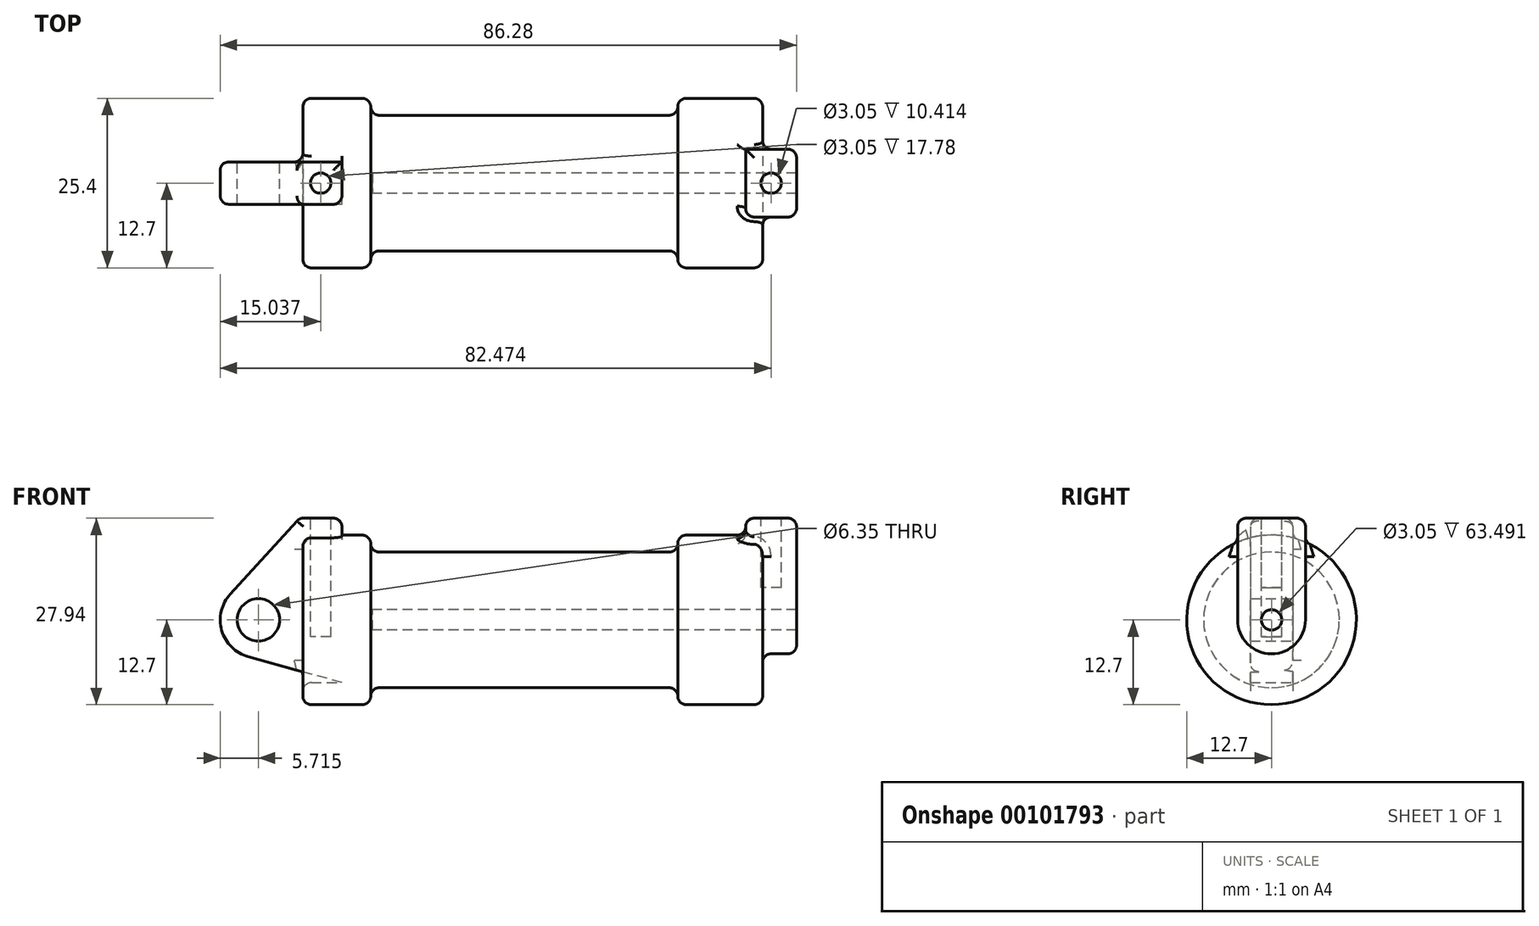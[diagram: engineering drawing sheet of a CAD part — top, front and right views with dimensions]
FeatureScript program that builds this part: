
annotation { "Feature Type Name" : "Feature", "Feature Type Description" : "" }
export const myFeature = defineFeature(function(context is Context, id is Id, definition is map)
    precondition{}
    {
        {
            var Q0;
            Q0=qCreatedBy(makeId("Front.planeOp"),FACE);
            var sketch = newSketch(context, id + "F0", { "sketchPlane" : qUnion([Q0])});
            skLineSegment(sketch, "E0", {"start": v(0, 0) * mm, "end": v(0, 12.7) * mm});
            skLineSegment(sketch, "E1", {"start": v(0, 12.7) * mm, "end": v(10.16, 12.7) * mm});
            skLineSegment(sketch, "E2", {"start": v(10.16, 12.7) * mm, "end": v(10.16, 10.16) * mm});
            skLineSegment(sketch, "E3", {"start": v(10.16, 10.16) * mm, "end": v(56.13, 10.16) * mm});
            skLineSegment(sketch, "E4", {"start": v(56.13, 10.16) * mm, "end": v(56.13, 12.7) * mm});
            skLineSegment(sketch, "E5", {"start": v(56.13, 12.7) * mm, "end": v(66.3, 12.7) * mm});
            skLineSegment(sketch, "E6", {"start": v(66.3, 12.7) * mm, "end": v(66.3, 0) * mm});
            skLineSegment(sketch, "E7", {"start": v(66.3, 0) * mm, "end": v(0, 0) * mm});
            skLineSegment(sketch, "E8", {"start": v(5.84, 15.24) * mm, "end": v(-0.5, 15.24) * mm});
            skLineSegment(sketch, "E9", {"start": v(-0.5, 15.24) * mm, "end": v(-10.88, 3.85) * mm});
            skLineSegment(sketch, "E10", {"start": v(0, 0) * mm, "end": v(-6.65, 0) * mm});
            skCircle(sketch, "E11", {"center": v(-6.65, 0) * mm, "radius": 5.72 * mm});
            skCircle(sketch, "E12", {"center": v(-6.65, 0) * mm, "radius": 3.18 * mm});
            skLineSegment(sketch, "E13", {"start": v(5.84, 15.24) * mm, "end": v(5.84, -9.4) * mm});
            skLineSegment(sketch, "E14", {"start": v(5.84, -9.4) * mm, "end": v(-8.18, -5.5) * mm});
            skSolve(sketch);
        }
        {
            var Q0;
            {var subQ0=sQuery(id+"F0.wireOp",EDGE,"E2");Q0=makeQuery(id+"F0.imprint","IMPRINT",FACE,{"disambiguationData":[TD([[makeQuery(id+"F0.imprint","IMPRINT",EDGE,{"derivedFrom":subQ0}),-1.0]])]});}
            var Q1;
            Q1=sQuery(id+"F0.wireOp",EDGE,"E7");
            revolve(context, id + "F1", {"entities" : qUnion([Q0]), "axis" : qUnion([Q1]), "revolveType" : RevolveType.FULL});
        }
        {
            var Q0;
            {var subQ3=sQuery(id+"F0.wireOp",EDGE,"E0");Q0=makeQuery(id+"F0.imprint","IMPRINT",FACE,{"disambiguationData":[TD([[makeQuery(id+"F0.imprint","IMPRINT",EDGE,{"derivedFrom":subQ3}),1.0]])]});}
            var Q1;
            {var subQ0=sQuery(id+"F0.wireOp",EDGE,"E0");Q1=makeQuery(id+"F0.imprint","IMPRINT",FACE,{"disambiguationData":[TD([[makeQuery(id+"F0.imprint","IMPRINT",EDGE,{"derivedFrom":subQ0}),-1.0]])]});}
            var Q2;
            {var subQ0=sQuery(id+"F0.wireOp",EDGE,"E14");Q2=makeQuery(id+"F0.imprint","IMPRINT",FACE,{"disambiguationData":[TD([[makeQuery(id+"F0.imprint","IMPRINT",EDGE,{"derivedFrom":subQ0}),-1.0]])]});}
            var Q3;
            {var subQ4=sQuery(id+"F0.wireOp",EDGE,"E12");Q3=makeQuery(id+"F0.imprint","IMPRINT",FACE,{"disambiguationData":[TD([[makeQuery(id+"F0.imprint","IMPRINT",EDGE,{"derivedFrom":subQ4}),-1.0]])]});}
            extrude(context, id + "F2", {"entities" : qUnion([Q0, Q1, Q2, Q3]), "operationType" : NewBodyOperationType.ADD, "depth" : 3.17 * mm, "hasSecondDirection" : true, "secondDirectionOppositeDirection" : true, "secondDirectionDepth" : 3.17 * mm});
        }
        {
            var Q0;
            Q0=makeQuery(id+"F1.opRevolve","SWEPT_FACE",FACE,{"disambiguationData":[OSD([sQuery(id+"F0.wireOp",EDGE,"E13")])]});
            extrude(context, id + "F3", {"entities" : qUnion([Q0]), "operationType" : NewBodyOperationType.ADD, "depth" : 5.84 * mm});
        }
        {
            var Q0;
            Q0=makeQuery(id+"F1.opRevolve","SWEPT_FACE",FACE,{"disambiguationData":[OSD([sQuery(id+"F0.wireOp",EDGE,"E6")])]});
            var sketch = newSketch(context, id + "F4", { "sketchPlane" : qUnion([Q0])});
            skCircle(sketch, "E15", {"center": v(0, 0) * mm, "radius": 1.52 * mm});
            skCircle(sketch, "E16", {"center": v(0, 0) * mm, "radius": 5.08 * mm});
            skLineSegment(sketch, "E17", {"start": v(-5.08, 0) * mm, "end": v(-5.08, 15.24) * mm});
            skLineSegment(sketch, "E18", {"start": v(-5.08, 15.24) * mm, "end": v(5.08, 15.24) * mm});
            skLineSegment(sketch, "E19", {"start": v(5.08, 15.24) * mm, "end": v(5.08, 0) * mm});
            skSolve(sketch);
        }
        {
            var Q0;
            Q0=makeQuery(id+"F4.imprint","IMPRINT",FACE,{"disambiguationData":[TD([[makeQuery(id+"F4.imprint","IMPRINT",EDGE,{"derivedFrom":sQuery(id+"F4.wireOp",EDGE,"E15")}),-1.0]])]});
            var Q1;
            {var subQ0=sQuery(id+"F4.wireOp",EDGE,"E17");var subQ1=sQuery(id+"F4.wireOp",EDGE,"E16");var subQ2=makeQuery(id+"F4.imprint","INTERSECT",VERTEX,{"derivedFrom":[subQ1,subQ0]});Q1=makeQuery(id+"F4.imprint","IMPRINT",FACE,{"disambiguationData":[TD([[makeQuery(id+"F4.imprint","IMPRINT",EDGE,{"disambiguationData":[TD([[subQ2,1.0]])],"derivedFrom":subQ1}),-1.0]])]});}
            var Q2;
            {var subQ0=sQuery(id+"F4.wireOp",EDGE,"E18");Q2=makeQuery(id+"F4.imprint","IMPRINT",FACE,{"disambiguationData":[TD([[makeQuery(id+"F4.imprint","IMPRINT",EDGE,{"derivedFrom":subQ0}),-1.0]])]});}
            extrude(context, id + "F5", {"entities" : qUnion([Q0, Q1, Q2]), "operationType" : NewBodyOperationType.ADD, "depth" : 7.62 * mm});
        }
        {
            var Q0;
            Q0=makeQuery(id+"F5.boolean.opBoolean","SPLIT",FACE,{"disambiguationData":[TD([makeQuery(id+"F1.opRevolve","SWEPT_FACE",FACE,{"disambiguationData":[OSD([sQuery(id+"F0.wireOp",EDGE,"E5")])]})])],"derivedFrom":makeQuery(id+"F1.opRevolve","SWEPT_FACE",FACE,{"disambiguationData":[OSD([sQuery(id+"F0.wireOp",EDGE,"E6")])]})});
            extrude(context, id + "F6", {"entities" : qUnion([Q0]), "operationType" : NewBodyOperationType.ADD, "depth" : 2.54 * mm});
        }
        {
            var Q0;
            Q0=makeQuery(id+"F5.boolean.opBoolean","SPLIT",FACE,{"disambiguationData":[TD([makeQuery(id+"F5.opExtrude","SWEPT_FACE",FACE,{"disambiguationData":[OSD([sQuery(id+"F4.wireOp",EDGE,"E15")])]})])],"derivedFrom":makeQuery(id+"F1.opRevolve","SWEPT_FACE",FACE,{"disambiguationData":[OSD([sQuery(id+"F0.wireOp",EDGE,"E6")])]})});
            extrude(context, id + "F7", {"entities" : qUnion([Q0]), "operationType" : NewBodyOperationType.REMOVE, "oppositeDirection" : true, "depth" : 55.87 * mm});
        }
        {
            var Q0;
            Q0=makeQuery(id+"F2.opExtrude","SWEPT_FACE",FACE,{"disambiguationData":[OSD([sQuery(id+"F0.wireOp",EDGE,"E8")])]});
            var sketch = newSketch(context, id + "F8", { "sketchPlane" : qUnion([Q0])});
            skCircle(sketch, "E20", {"center": v(2.67, 0) * mm, "radius": 1.52 * mm});
            skPoint(sketch, "E20.centerSnap0", {"position": v(5.84, 0) * mm});
            skPoint(sketch, "E20.centerSnap1", {"position": v(2.67, 3.18) * mm});
            skSolve(sketch);
        }
        {
            var Q0;
            Q0=makeQuery(id+"F5.opExtrude","SWEPT_FACE",FACE,{"disambiguationData":[OSD([sQuery(id+"F4.wireOp",EDGE,"E18")])]});
            var sketch = newSketch(context, id + "F9", { "sketchPlane" : qUnion([Q0])});
            skCircle(sketch, "E21", {"center": v(70.1, 0) * mm, "radius": 1.52 * mm});
            skPoint(sketch, "E21.centerSnap0", {"position": v(73.91, 0) * mm});
            skPoint(sketch, "E21.centerSnap1", {"position": v(70.1, 5.08) * mm});
            skSolve(sketch);
        }
        {
            var Q0;
            Q0=makeQuery(id+"F9.imprint","IMPRINT",FACE,{"disambiguationData":[TD([[makeQuery(id+"F9.imprint","IMPRINT",EDGE,{"derivedFrom":sQuery(id+"F9.wireOp",EDGE,"E21")}),1.0]])]});
            extrude(context, id + "F10", {"entities" : qUnion([Q0]), "operationType" : NewBodyOperationType.REMOVE, "oppositeDirection" : true, "depth" : 10.4 * mm});
        }
        {
            var Q0;
            Q0=makeQuery(id+"F8.imprint","IMPRINT",FACE,{"disambiguationData":[TD([[makeQuery(id+"F8.imprint","IMPRINT",EDGE,{"derivedFrom":sQuery(id+"F8.wireOp",EDGE,"E20")}),1.0]])]});
            extrude(context, id + "F11", {"entities" : qUnion([Q0]), "operationType" : NewBodyOperationType.REMOVE, "oppositeDirection" : true, "depth" : 17.78 * mm});
        }
        {
            var Q0;
            Q0=makeQuery(id+"F2.opExtrude","CAP_EDGE",EDGE,{"disambiguationData":[OSD([sQuery(id+"F0.wireOp",EDGE,"E9")])],"isStart":false});
            var Q1;
            Q1=makeQuery(id+"F2.opExtrude","CAP_EDGE",EDGE,{"disambiguationData":[OSD([sQuery(id+"F0.wireOp",EDGE,"E11")])],"isStart":false});
            var Q2;
            {var subQ0=sQuery(id+"F0.wireOp",EDGE,"E14");Q2=makeQuery(id+"F3.boolean.opBoolean","SPLIT",EDGE,{"disambiguationData":[topologyDisambiguationEdgeConnected([makeQuery(id+"F2.opExtrude","CAP_FACE",FACE,{"disambiguationData":[OSD([sQuery(id+"F0.wireOp",EDGE,"E8"),sQuery(id+"F0.wireOp",EDGE,"E9"),sQuery(id+"F0.wireOp",EDGE,"E11"),sQuery(id+"F0.wireOp",EDGE,"E12"),sQuery(id+"F0.wireOp",EDGE,"E13"),subQ0])],"isStart":false})])],"derivedFrom":makeQuery(id+"F2.opExtrude","CAP_EDGE",EDGE,{"disambiguationData":[OSD([subQ0])],"isStart":false})});}
            var Q3;
            Q3=makeQuery(id+"F3.opExtrude","CAP_EDGE",EDGE,{"disambiguationData":[OSD([sQuery(id+"F0.wireOp",EDGE,"E1"),sQuery(id+"F0.wireOp",EDGE,"E13")])],"isStart":false});
            var Q4;
            Q4=makeQuery(id+"F1.opRevolve","SWEPT_EDGE",EDGE,{"disambiguationData":[OSD([sQuery(id+"F0.wireOp",EDGE,"E1"),sQuery(id+"F0.wireOp",EDGE,"E2")])]});
            fillet(context, id + "F12", {"entities" : qUnion([Q0, Q1, Q2, Q3, Q4]), "radius" : 1.27 * mm, "tangentPropagation" : true, "allowEdgeOverflow" : false});
        }
        {
            var Q0;
            Q0=makeQuery(id+"F2.opExtrude","CAP_EDGE",EDGE,{"disambiguationData":[OSD([sQuery(id+"F0.wireOp",EDGE,"E9")])],"isStart":true});
            var Q1;
            Q1=makeQuery(id+"F2.opExtrude","CAP_EDGE",EDGE,{"disambiguationData":[OSD([sQuery(id+"F0.wireOp",EDGE,"E11")])],"isStart":true});
            var Q2;
            {var subQ0=sQuery(id+"F0.wireOp",EDGE,"E14");Q2=makeQuery(id+"F3.boolean.opBoolean","SPLIT",EDGE,{"disambiguationData":[topologyDisambiguationEdgeConnected([makeQuery(id+"F2.opExtrude","CAP_FACE",FACE,{"disambiguationData":[OSD([sQuery(id+"F0.wireOp",EDGE,"E8"),sQuery(id+"F0.wireOp",EDGE,"E9"),sQuery(id+"F0.wireOp",EDGE,"E11"),sQuery(id+"F0.wireOp",EDGE,"E12"),sQuery(id+"F0.wireOp",EDGE,"E13"),subQ0])],"isStart":true})])],"derivedFrom":makeQuery(id+"F2.opExtrude","CAP_EDGE",EDGE,{"disambiguationData":[OSD([subQ0])],"isStart":true})});}
            var Q3;
            Q3=makeQuery(id+"F2.opExtrude","CAP_EDGE",EDGE,{"disambiguationData":[OSD([sQuery(id+"F0.wireOp",EDGE,"E8")])],"isStart":true});
            var Q4;
            Q4=makeQuery(id+"F2.opExtrude","SWEPT_EDGE",EDGE,{"disambiguationData":[OSD([sQuery(id+"F0.wireOp",EDGE,"E8"),sQuery(id+"F0.wireOp",EDGE,"E13")])]});
            var Q5;
            {var subQ0=sQuery(id+"F0.wireOp",EDGE,"E1");var subQ1=sQuery(id+"F0.wireOp",EDGE,"E13");Q5=makeQuery(id+"F2.boolean.opBoolean","SPLIT",EDGE,{"disambiguationData":[topologyDisambiguationEdgeConnected([makeQuery(id+"F2.opExtrude","SWEPT_FACE",FACE,{"disambiguationData":[OSD([subQ1])]})])],"derivedFrom":makeQuery(id+"F1.opRevolve","SWEPT_EDGE",EDGE,{"disambiguationData":[OSD([subQ0,subQ1])]})});}
            fillet(context, id + "F13", {"entities" : qUnion([Q0, Q1, Q2, Q3, Q4, Q5]), "radius" : 1.27 * mm, "tangentPropagation" : true, "allowEdgeOverflow" : false});
        }
        {
            var Q0;
            Q0=makeQuery(id+"F2.opExtrude","CAP_EDGE",EDGE,{"disambiguationData":[OSD([sQuery(id+"F0.wireOp",EDGE,"E8")])],"isStart":false});
            var Q1;
            Q1=makeQuery(id+"F1.opRevolve","SWEPT_EDGE",EDGE,{"disambiguationData":[OSD([sQuery(id+"F0.wireOp",EDGE,"E4"),sQuery(id+"F0.wireOp",EDGE,"E5")])]});
            var Q2;
            Q2=makeQuery(id+"F6.opExtrude","CAP_EDGE",EDGE,{"disambiguationData":[OSD([sQuery(id+"F0.wireOp",EDGE,"E5"),sQuery(id+"F0.wireOp",EDGE,"E6")])],"isStart":false});
            var Q3;
            {var subQ0=sQuery(id+"F4.wireOp",EDGE,"E17");Q3=makeQuery(id+"F5.boolean.opBoolean","SPLIT",EDGE,{"disambiguationData":[topologyDisambiguationEdgeConnected([makeQuery(id+"F5.opExtrude","CAP_FACE",FACE,{"disambiguationData":[OSD([sQuery(id+"F4.wireOp",EDGE,"E15"),sQuery(id+"F4.wireOp",EDGE,"E16"),subQ0,sQuery(id+"F4.wireOp",EDGE,"E18"),sQuery(id+"F4.wireOp",EDGE,"E19")])],"isStart":true})])],"derivedFrom":makeQuery(id+"F5.opExtrude","CAP_EDGE",EDGE,{"disambiguationData":[OSD([subQ0])],"isStart":true})});}
            var Q4;
            Q4=makeQuery(id+"F5.opExtrude","CAP_EDGE",EDGE,{"disambiguationData":[OSD([sQuery(id+"F4.wireOp",EDGE,"E16")])],"isStart":false});
            var Q5;
            Q5=makeQuery(id+"F5.opExtrude","CAP_EDGE",EDGE,{"disambiguationData":[OSD([sQuery(id+"F4.wireOp",EDGE,"E17")])],"isStart":false});
            var Q6;
            Q6=makeQuery(id+"F5.opExtrude","CAP_EDGE",EDGE,{"disambiguationData":[OSD([sQuery(id+"F4.wireOp",EDGE,"E19")])],"isStart":false});
            var Q7;
            Q7=makeQuery(id+"F5.opExtrude","CAP_EDGE",EDGE,{"disambiguationData":[OSD([sQuery(id+"F4.wireOp",EDGE,"E18")])],"isStart":false});
            var Q8;
            Q8=makeQuery(id+"F5.opExtrude","SWEPT_EDGE",EDGE,{"disambiguationData":[OSD([sQuery(id+"F4.wireOp",EDGE,"E17"),sQuery(id+"F4.wireOp",EDGE,"E18")])]});
            var Q9;
            Q9=makeQuery(id+"F5.opExtrude","CAP_EDGE",EDGE,{"disambiguationData":[OSD([sQuery(id+"F4.wireOp",EDGE,"E18")])],"isStart":true});
            var Q10;
            Q10=makeQuery(id+"F5.opExtrude","SWEPT_EDGE",EDGE,{"disambiguationData":[OSD([sQuery(id+"F4.wireOp",EDGE,"E18"),sQuery(id+"F4.wireOp",EDGE,"E19")])]});
            fillet(context, id + "F14", {"entities" : qUnion([Q0, Q1, Q2, Q3, Q4, Q5, Q6, Q7, Q8, Q9, Q10]), "radius" : 1.27 * mm, "tangentPropagation" : true, "allowEdgeOverflow" : false});
        }
        {
            var Q0;
            Q0=makeQuery(id+"F1.opRevolve","SWEPT_EDGE",EDGE,{"disambiguationData":[OSD([sQuery(id+"F0.wireOp",EDGE,"E3"),sQuery(id+"F0.wireOp",EDGE,"E4")])]});
            var Q1;
            Q1=makeQuery(id+"F1.opRevolve","SWEPT_EDGE",EDGE,{"disambiguationData":[OSD([sQuery(id+"F0.wireOp",EDGE,"E2"),sQuery(id+"F0.wireOp",EDGE,"E3")])]});
            fillet(context, id + "F15", {"entities" : qUnion([Q0, Q1]), "radius" : 1.27 * mm, "tangentPropagation" : true, "allowEdgeOverflow" : false});
        }
        {
            var Q0;
            Q0=makeQuery(id+"F14.opFillet","BLEND_EDGE",EDGE,{"blendedFrom":[makeQuery(id+"F6.opExtrude","CAP_EDGE",EDGE,{"disambiguationData":[OSD([sQuery(id+"F0.wireOp",EDGE,"E5"),sQuery(id+"F0.wireOp",EDGE,"E6")])],"isStart":false}),makeQuery(id+"F5.opExtrude","SWEPT_FACE",FACE,{"disambiguationData":[OSD([sQuery(id+"F4.wireOp",EDGE,"E17")])]})],"blendedInto":[makeQuery(id+"F5.opExtrude","SWEPT_FACE",FACE,{"disambiguationData":[OSD([sQuery(id+"F4.wireOp",EDGE,"E17")])]})]});
            var Q1;
            {var subQ0=sQuery(id+"F0.wireOp",EDGE,"E13");Q1=makeQuery(id+"F12.opFillet","BLEND_EDGE",EDGE,{"blendedFrom":[makeQuery(id+"F3.opExtrude","CAP_EDGE",EDGE,{"disambiguationData":[OSD([sQuery(id+"F0.wireOp",EDGE,"E1"),subQ0])],"isStart":false}),makeQuery(id+"F2.opExtrude","CAP_FACE",FACE,{"disambiguationData":[OSD([sQuery(id+"F0.wireOp",EDGE,"E8"),sQuery(id+"F0.wireOp",EDGE,"E9"),sQuery(id+"F0.wireOp",EDGE,"E11"),sQuery(id+"F0.wireOp",EDGE,"E12"),subQ0,sQuery(id+"F0.wireOp",EDGE,"E14")])],"isStart":true})],"blendedInto":[makeQuery(id+"F2.opExtrude","CAP_FACE",FACE,{"disambiguationData":[OSD([sQuery(id+"F0.wireOp",EDGE,"E8"),sQuery(id+"F0.wireOp",EDGE,"E9"),sQuery(id+"F0.wireOp",EDGE,"E11"),sQuery(id+"F0.wireOp",EDGE,"E12"),subQ0,sQuery(id+"F0.wireOp",EDGE,"E14")])],"isStart":true})]});}
            var Q2;
            Q2=makeQuery(id+"F3.opExtrude","CAP_EDGE",EDGE,{"disambiguationData":[OSD([sQuery(id+"F0.wireOp",EDGE,"E13"),sQuery(id+"F0.wireOp",EDGE,"E14")])],"isStart":false});
            fillet(context, id + "F16", {"entities" : qUnion([Q0, Q1, Q2]), "radius" : 1.27 * mm, "tangentPropagation" : true, "allowEdgeOverflow" : false});
        }
    });
